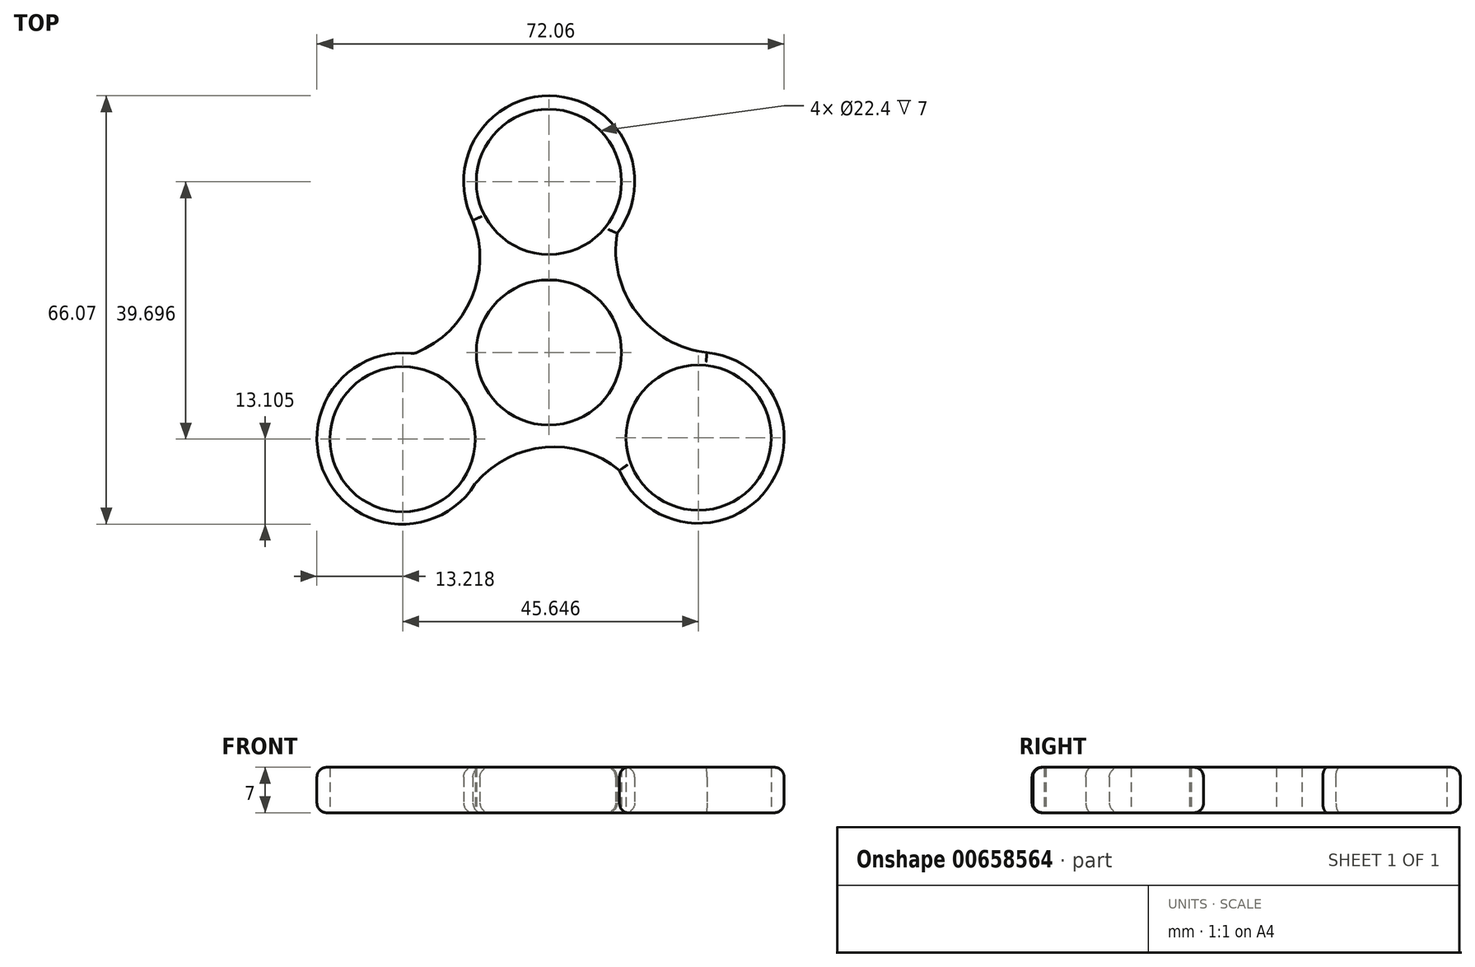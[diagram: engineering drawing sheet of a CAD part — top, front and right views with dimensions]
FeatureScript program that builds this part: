
annotation { "Feature Type Name" : "Feature", "Feature Type Description" : "" }
export const myFeature = defineFeature(function(context is Context, id is Id, definition is map)
    precondition{}
    {
        {
            var Q0;
            Q0=qCreatedBy(makeId("Top.planeOp"),FACE);
            var sketch = newSketch(context, id + "F0", { "sketchPlane" : qUnion([Q0])});
            skCircle(sketch, "E0", {"center": v(0, 0) * mm, "radius": 11.2 * mm});
            skSolve(sketch);
        }
        {
            var Q0;
            Q0=qCreatedBy(makeId("Top.planeOp"),FACE);
            var sketch = newSketch(context, id + "F1", { "sketchPlane" : qUnion([Q0])});
            skCircle(sketch, "E1", {"center": v(-22.56, -13.36) * mm, "radius": 11.2 * mm});
            skCircle(sketch, "E2", {"center": v(23.08, -13.14) * mm, "radius": 11.2 * mm});
            skArc(sketch, "E3", {"start": v(10.89, -18.19) * mm, "mid": v(33.69, -21) * mm, "end": v(24.38, 0) * mm});
            skCircle(sketch, "E4", {"center": v(0, 26.33) * mm, "radius": 11.2 * mm});
            skArc(sketch, "E5", {"start": v(10.53, 18.4) * mm, "mid": v(13.5, 6.22) * mm, "end": v(24.38, 0) * mm});
            skArc(sketch, "E6.1.0", {"start": v(-20.97, -0.2) * mm, "mid": v(-11.9, 8.45) * mm, "end": v(-11.96, 20.98) * mm});
            skArc(sketch, "E6.2.0", {"start": v(10.89, -18.19) * mm, "mid": v(-1.14, -14.67) * mm, "end": v(-11.96, -20.98) * mm});
            skArc(sketch, "E7.trimOffspring", {"start": v(10.53, 18.4) * mm, "mid": v(1.22, 39.54) * mm, "end": v(-11.72, 20.4) * mm});
            skArc(sketch, "E8.trimOffspring", {"start": v(-20.9, -0.18) * mm, "mid": v(-34.5, -18.96) * mm, "end": v(-11.35, -20.2) * mm});
            skSolve(sketch);
        }
        {
            var Q0;
            Q0=makeQuery(id+"F1.imprint","IMPRINT",FACE,{"disambiguationData":[TD([[makeQuery(id+"F1.imprint","IMPRINT",EDGE,{"derivedFrom":sQuery(id+"F1.wireOp",EDGE,"E1")}),-1.0]])]});
            extrude(context, id + "F2", {"entities" : qUnion([Q0]), "depth" : 7 * mm, "offsetDistance" : 25 * mm});
        }
        {
            var Q0;
            Q0=sQuery(id+"F0.wireOp",VERTEX,"E0.center");
            var Q1;
            Q1=makeQuery(id+"F2.opExtrude","SWEPT_BODY",BODY,{"disambiguationData":[OSD([sQuery(id+"F1.wireOp",EDGE,"E1"),sQuery(id+"F1.wireOp",EDGE,"E2"),sQuery(id+"F1.wireOp",EDGE,"E3"),sQuery(id+"F1.wireOp",EDGE,"E4"),sQuery(id+"F1.wireOp",EDGE,"E5"),sQuery(id+"F1.wireOp",EDGE,"E6.1.0"),sQuery(id+"F1.wireOp",EDGE,"E6.2.0"),sQuery(id+"F1.wireOp",EDGE,"E7.trimOffspring"),sQuery(id+"F1.wireOp",EDGE,"E8.trimOffspring")])]});
            hole(context, id + "F3", {"style" : HoleStyle.SIMPLE, "endStyle" : HoleEndStyle.THROUGH, "oppositeDirection" : true, "holeDiameter" : 22.4 * mm, "majorDiameter" : 5 * mm, "isTappedThrough" : true, "tappedDepth" : 12 * mm, "tapClearance" : 3, "locations" : qUnion([Q0]), "scope" : qUnion([Q1])});
        }
        {
            var Q0;
            Q0=makeQuery(id+"F2.opExtrude","CAP_EDGE",EDGE,{"disambiguationData":[OSD([sQuery(id+"F1.wireOp",EDGE,"E6.2.0")])],"isStart":false});
            var Q1;
            Q1=makeQuery(id+"F2.opExtrude","CAP_EDGE",EDGE,{"disambiguationData":[OSD([sQuery(id+"F1.wireOp",EDGE,"E6.2.0")])],"isStart":true});
            var Q2;
            Q2=makeQuery(id+"F2.opExtrude","CAP_EDGE",EDGE,{"disambiguationData":[OSD([sQuery(id+"F1.wireOp",EDGE,"E8.trimOffspring")])],"isStart":false});
            var Q3;
            Q3=makeQuery(id+"F2.opExtrude","SWEPT_FACE",FACE,{"disambiguationData":[OSD([sQuery(id+"F1.wireOp",EDGE,"E8.trimOffspring")])]});
            var Q4;
            Q4=makeQuery(id+"F2.opExtrude","CAP_EDGE",EDGE,{"disambiguationData":[OSD([sQuery(id+"F1.wireOp",EDGE,"E6.1.0")])],"isStart":false});
            var Q5;
            Q5=makeQuery(id+"F2.opExtrude","CAP_EDGE",EDGE,{"disambiguationData":[OSD([sQuery(id+"F1.wireOp",EDGE,"E3")])],"isStart":false});
            var Q6;
            Q6=makeQuery(id+"F2.opExtrude","CAP_EDGE",EDGE,{"disambiguationData":[OSD([sQuery(id+"F1.wireOp",EDGE,"E3")])],"isStart":true});
            var Q7;
            Q7=makeQuery(id+"F2.opExtrude","CAP_EDGE",EDGE,{"disambiguationData":[OSD([sQuery(id+"F1.wireOp",EDGE,"E5")])],"isStart":false});
            var Q8;
            Q8=makeQuery(id+"F2.opExtrude","CAP_EDGE",EDGE,{"disambiguationData":[OSD([sQuery(id+"F1.wireOp",EDGE,"E7.trimOffspring")])],"isStart":false});
            var Q9;
            Q9=makeQuery(id+"F2.opExtrude","CAP_EDGE",EDGE,{"disambiguationData":[OSD([sQuery(id+"F1.wireOp",EDGE,"E7.trimOffspring")])],"isStart":true});
            var Q10;
            Q10=makeQuery(id+"F2.opExtrude","CAP_EDGE",EDGE,{"disambiguationData":[OSD([sQuery(id+"F1.wireOp",EDGE,"E5")])],"isStart":true});
            var Q11;
            Q11=makeQuery(id+"F2.opExtrude","CAP_EDGE",EDGE,{"disambiguationData":[OSD([sQuery(id+"F1.wireOp",EDGE,"E6.1.0")])],"isStart":true});
            fillet(context, id + "F4", {"entities" : qUnion([Q0, Q1, Q2, Q3, Q4, Q5, Q6, Q7, Q8, Q9, Q10, Q11]), "radius" : 1.5 * mm, "tangentPropagation" : true, "allowEdgeOverflow" : false});
        }
    });
